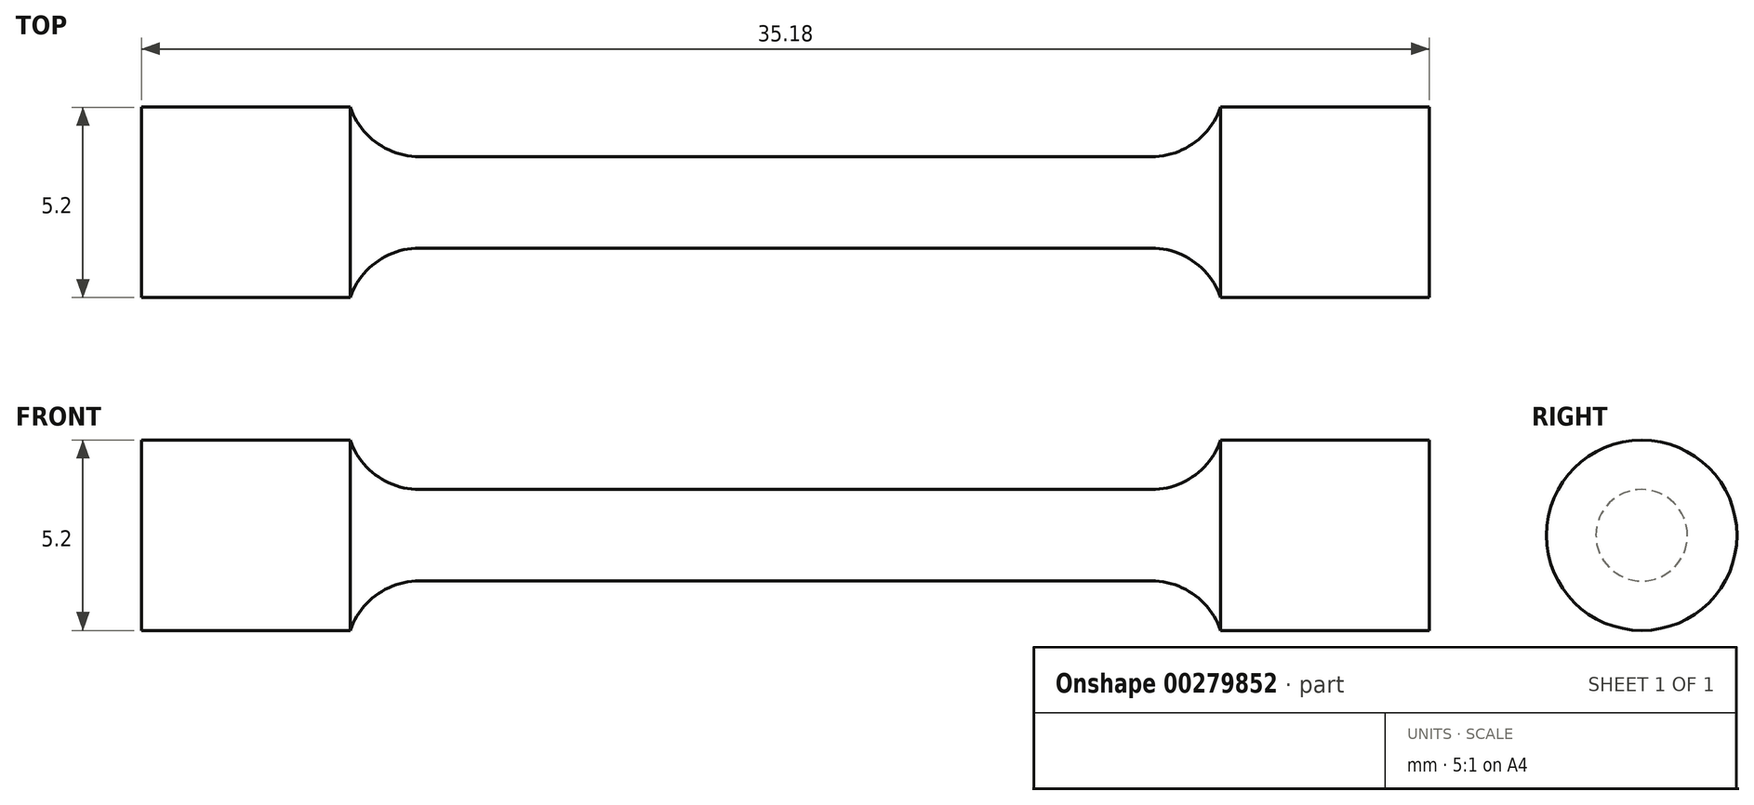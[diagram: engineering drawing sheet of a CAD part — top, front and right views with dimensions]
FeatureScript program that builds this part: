
annotation { "Feature Type Name" : "Feature", "Feature Type Description" : "" }
export const myFeature = defineFeature(function(context is Context, id is Id, definition is map)
    precondition{}
    {
        {
            var Q0;
            Q0=qCreatedBy(makeId("Front.planeOp"),FACE);
            var sketch = newSketch(context, id + "F0", { "sketchPlane" : qUnion([Q0])});
            skLineSegment(sketch, "E0", {"start": v(0, 1.25) * mm, "end": v(10, 1.25) * mm});
            skArc(sketch, "E1", {"start": v(10, 1.25) * mm, "mid": v(11.16, 1.62) * mm, "end": v(11.9, 2.6) * mm});
            skLineSegment(sketch, "E2", {"start": v(11.9, 2.6) * mm, "end": v(17.6, 2.6) * mm});
            skLineSegment(sketch, "E3", {"start": v(17.6, 2.6) * mm, "end": v(17.6, 0) * mm});
            skLineSegment(sketch, "E4.MirrorCS", {"start": v(0, 1.25) * mm, "end": v(-10, 1.25) * mm});
            skLineSegment(sketch, "E5.MirrorCS", {"start": v(-11.9, 2.6) * mm, "end": v(-17.6, 2.6) * mm});
            skArc(sketch, "E6.MirrorCS", {"start": v(-10, 1.25) * mm, "mid": v(-11.16, 1.62) * mm, "end": v(-11.9, 2.6) * mm});
            skLineSegment(sketch, "E7.MirrorCS", {"start": v(-17.6, 2.6) * mm, "end": v(-17.6, 0) * mm});
            skLineSegment(sketch, "E8", {"start": v(-17.6, 0) * mm, "end": v(17.6, 0) * mm});
            skSolve(sketch);
        }
        {
            var Q0;
            Q0=makeQuery(id+"F0.imprint","IMPRINT",FACE,{"disambiguationData":[TD([[makeQuery(id+"F0.imprint","IMPRINT",EDGE,{"derivedFrom":sQuery(id+"F0.wireOp",EDGE,"E0")}),-1.0]])]});
            var Q1;
            Q1=sQuery(id+"F0.wireOp",EDGE,"E8");
            revolve(context, id + "F1", {"entities" : qUnion([Q0]), "axis" : qUnion([Q1]), "revolveType" : RevolveType.FULL});
        }
    });
